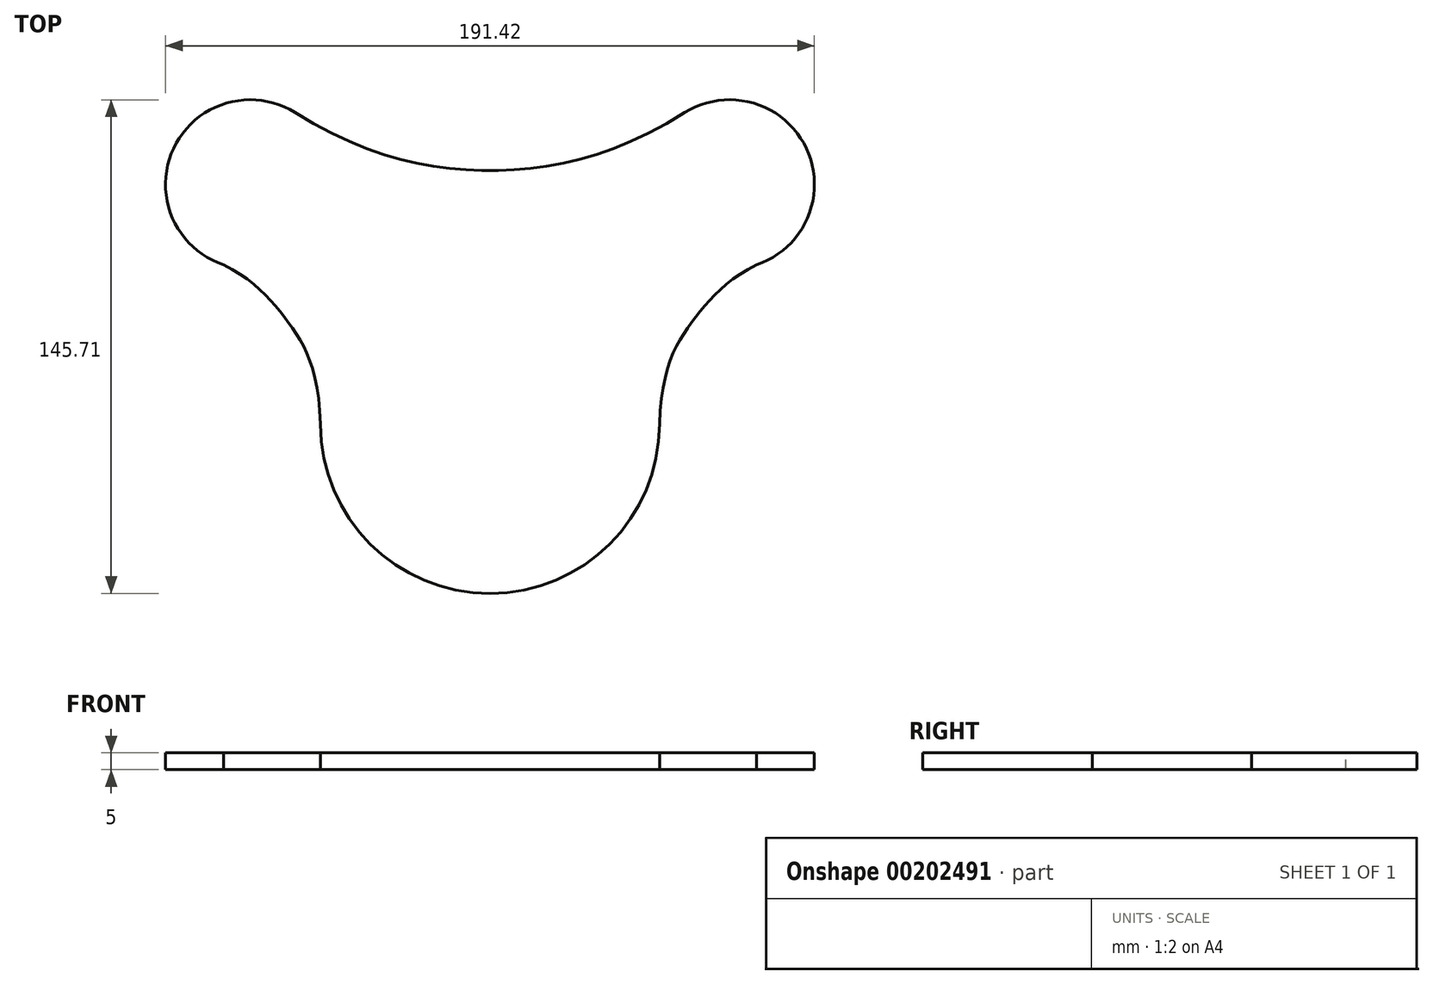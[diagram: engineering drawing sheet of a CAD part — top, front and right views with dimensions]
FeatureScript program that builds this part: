
annotation { "Feature Type Name" : "Feature", "Feature Type Description" : "" }
export const myFeature = defineFeature(function(context is Context, id is Id, definition is map)
    precondition{}
    {
        {
            var Q0;
            Q0=qCreatedBy(makeId("Top.planeOp"),FACE);
            var sketch = newSketch(context, id + "F0", { "sketchPlane" : qUnion([Q0])});
            skCircle(sketch, "E0", {"center": v(0, 0) * mm, "radius": 50 * mm});
            skCircle(sketch, "E1", {"center": v(-70.71, 70.71) * mm, "radius": 25 * mm});
            skCircle(sketch, "E2.MirrorC", {"center": v(70.71, 70.71) * mm, "radius": 25 * mm});
            skLineSegment(sketch, "E3", {"start": v(-70.71, 70.71) * mm, "end": v(0, 0) * mm, "construction": true});
            skLineSegment(sketch, "E4", {"start": v(-43.07, -25.4) * mm, "end": v(-92.25, 58.01) * mm, "construction": true});
            skLineSegment(sketch, "E5.MirrorCS", {"start": v(43.07, -25.4) * mm, "end": v(92.25, 58.01) * mm, "construction": true});
            skFitSpline(sketch, "E6", {"points": [v(-57.47, 91.92) * mm, v(0, 74.85) * mm, v(57.47, 91.92) * mm], "startDerivative": vector(126.15, -78.74) * mm, "endDerivative": vector(126.15, 78.74) * mm});
            skLineSegment(sketch, "E7", {"start": v(-57.47, 91.92) * mm, "end": v(57.47, 91.92) * mm, "construction": true});
            skLineSegment(sketch, "E8", {"start": v(0, 74.85) * mm, "end": v(-32.88, 74.85) * mm, "construction": true});
            skLineSegment(sketch, "E9", {"start": v(0, 74.85) * mm, "end": v(36.15, 74.85) * mm, "construction": true});
            skFitSpline(sketch, "E10", {"points": [v(83.04, 48.96) * mm, v(60.19, 30.9) * mm, v(49.93, -2.7) * mm], "startDerivative": vector(-76.34, -30.14) * mm, "endDerivative": vector(-1.8, -111.03) * mm});
            skFitSpline(sketch, "E11.MirrorCS", {"points": [v(-83.04, 48.96) * mm, v(-60.19, 30.9) * mm, v(-49.93, -2.7) * mm], "startDerivative": vector(76.34, -30.14) * mm, "endDerivative": vector(1.8, -111.03) * mm});
            skSolve(sketch);
        }
        {
            var Q0;
            Q0 = qSketchRegion(id + "F0", true);
            extrude(context, id + "F1", {"entities" : qUnion([Q0]), "depth" : 5 * mm});
        }
    });
